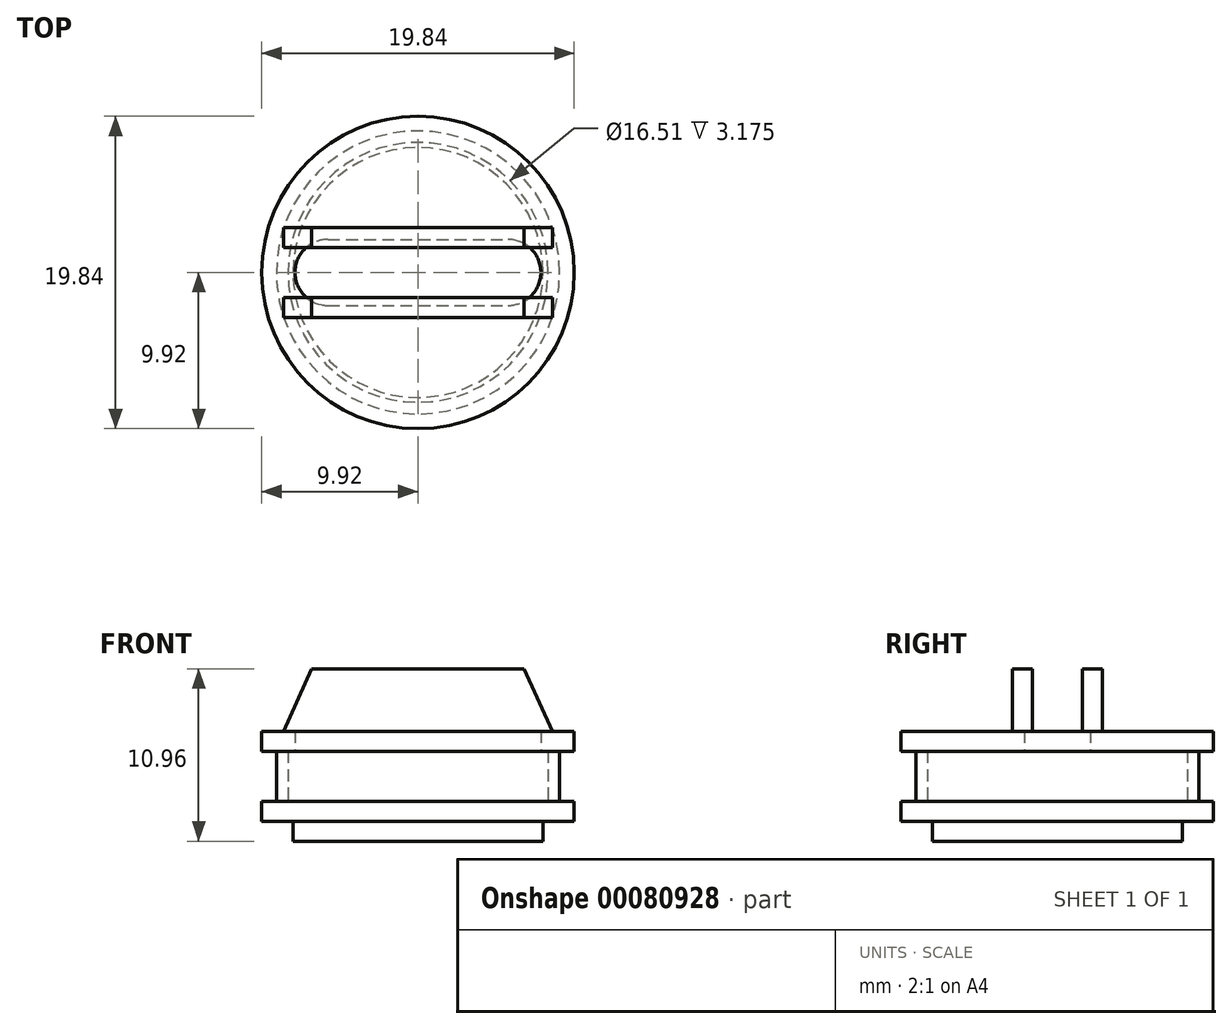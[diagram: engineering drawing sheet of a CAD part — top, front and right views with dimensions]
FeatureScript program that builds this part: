
annotation { "Feature Type Name" : "Feature", "Feature Type Description" : "" }
export const myFeature = defineFeature(function(context is Context, id is Id, definition is map)
    precondition{}
    {
        {
            var Q0;
            Q0=qCreatedBy(makeId("Top.planeOp"),FACE);
            var sketch = newSketch(context, id + "F0", { "sketchPlane" : qUnion([Q0])});
            skCircle(sketch, "E0", {"center": v(0, 0) * mm, "radius": 9.92 * mm});
            skCircle(sketch, "E1", {"center": v(0, 0) * mm, "radius": 9 * mm});
            skCircle(sketch, "E2", {"center": v(0, 0) * mm, "radius": 8.26 * mm});
            skLineSegment(sketch, "E3", {"start": v(-5.72, 2.1) * mm, "end": v(5.72, 2.1) * mm});
            skLineSegment(sketch, "E4", {"start": v(-5.72, -2.1) * mm, "end": v(5.72, -2.1) * mm});
            skArc(sketch, "E5", {"start": v(-5.72, 2.1) * mm, "mid": v(-7.81, 0) * mm, "end": v(-5.72, -2.1) * mm});
            skArc(sketch, "E6", {"start": v(5.72, 2.1) * mm, "mid": v(7.81, 0) * mm, "end": v(5.72, -2.1) * mm});
            skLineSegment(sketch, "E7", {"start": v(-5.72, 0) * mm, "end": v(5.72, 0) * mm, "construction": true});
            skSolve(sketch);
        }
        {
            var Q0;
            Q0=makeQuery(id+"F0.imprint","IMPRINT",FACE,{"disambiguationData":[TD([[makeQuery(id+"F0.imprint","IMPRINT",EDGE,{"derivedFrom":sQuery(id+"F0.wireOp",EDGE,"E0")}),1.0]])]});
            var Q1;
            Q1=makeQuery(id+"F0.imprint","IMPRINT",FACE,{"disambiguationData":[TD([[makeQuery(id+"F0.imprint","IMPRINT",EDGE,{"derivedFrom":sQuery(id+"F0.wireOp",EDGE,"E1")}),1.0]])]});
            var Q2;
            Q2=makeQuery(id+"F0.imprint","IMPRINT",FACE,{"disambiguationData":[TD([[makeQuery(id+"F0.imprint","IMPRINT",EDGE,{"derivedFrom":sQuery(id+"F0.wireOp",EDGE,"E2")}),1.0]])]});
            var Q3;
            Q3=makeQuery(id+"F0.imprint","IMPRINT",FACE,{"disambiguationData":[TD([[makeQuery(id+"F0.imprint","IMPRINT",EDGE,{"derivedFrom":sQuery(id+"F0.wireOp",EDGE,"E3")}),-1.0]])]});
            extrude(context, id + "F1", {"entities" : qUnion([Q0, Q1, Q2, Q3]), "oppositeDirection" : true, "depth" : 1.27 * mm});
        }
        {
            var Q0;
            Q0=makeQuery(id+"F1.opExtrude","CAP_FACE",FACE,{"disambiguationData":[OSD([sQuery(id+"F0.wireOp",EDGE,"E0")])],"isStart":false});
            cPlane(context, id + "F2", {"entities" : qUnion([Q0]), "cplaneType" : CPlaneType.OFFSET, "offset" : 0 * mm, "width" : 152.4 * mm, "height" : 152.4 * mm});
        }
        {
            var Q0;
            Q0=qCreatedBy(id+"F2.planeOp",FACE);
            var sketch = newSketch(context, id + "F3", { "sketchPlane" : qUnion([Q0])});
            skCircle(sketch, "E8", {"center": v(0, 0) * mm, "radius": 7.94 * mm});
            skSolve(sketch);
        }
        {
            var Q0;
            Q0=makeQuery(id+"F3.imprint","IMPRINT",FACE,{"disambiguationData":[TD([[makeQuery(id+"F3.imprint","IMPRINT",EDGE,{"derivedFrom":sQuery(id+"F3.wireOp",EDGE,"E8")}),1.0]])]});
            extrude(context, id + "F4", {"entities" : qUnion([Q0]), "depth" : 1.27 * mm});
        }
        {
            var Q0;
            Q0=makeQuery(id+"F0.imprint","IMPRINT",FACE,{"disambiguationData":[TD([[makeQuery(id+"F0.imprint","IMPRINT",EDGE,{"derivedFrom":sQuery(id+"F0.wireOp",EDGE,"E1")}),1.0]])]});
            extrude(context, id + "F5", {"entities" : qUnion([Q0]), "depth" : 3.17 * mm});
        }
        {
            var Q0;
            Q0=makeQuery(id+"F5.opExtrude","CAP_FACE",FACE,{"disambiguationData":[OSD([sQuery(id+"F0.wireOp",EDGE,"E1"),sQuery(id+"F0.wireOp",EDGE,"E2")])],"isStart":false});
            cPlane(context, id + "F6", {"entities" : qUnion([Q0]), "cplaneType" : CPlaneType.OFFSET, "offset" : 0 * mm, "width" : 152.4 * mm, "height" : 152.4 * mm});
        }
        {
            var Q0;
            Q0=qCreatedBy(id+"F6.planeOp",FACE);
            var sketch = newSketch(context, id + "F7", { "sketchPlane" : qUnion([Q0])});
            skCircle(sketch, "E9", {"center": v(0, 0) * mm, "radius": 9.92 * mm});
            skLineSegment(sketch, "E10", {"start": v(-5.72, 2.1) * mm, "end": v(5.72, 2.1) * mm});
            skLineSegment(sketch, "E11", {"start": v(-5.72, -2.1) * mm, "end": v(5.72, -2.1) * mm});
            skArc(sketch, "E12", {"start": v(-5.72, 2.1) * mm, "mid": v(-7.81, 0) * mm, "end": v(-5.72, -2.1) * mm});
            skArc(sketch, "E13", {"start": v(5.72, 2.1) * mm, "mid": v(7.81, 0) * mm, "end": v(5.72, -2.1) * mm});
            skLineSegment(sketch, "E14", {"start": v(-5.72, 0) * mm, "end": v(5.72, 0) * mm, "construction": true});
            skSolve(sketch);
        }
        {
            var Q0;
            Q0=makeQuery(id+"F7.imprint","IMPRINT",FACE,{"disambiguationData":[TD([[makeQuery(id+"F7.imprint","IMPRINT",EDGE,{"derivedFrom":sQuery(id+"F7.wireOp",EDGE,"E9")}),1.0]])]});
            extrude(context, id + "F8", {"entities" : qUnion([Q0]), "depth" : 1.27 * mm});
        }
        {
            var Q0;
            Q0=qCreatedBy(makeId("Front.planeOp"),FACE);
            cPlane(context, id + "F9", {"entities" : qUnion([Q0]), "cplaneType" : CPlaneType.OFFSET, "offset" : 1.59 * mm, "width" : 152.4 * mm, "height" : 152.4 * mm});
        }
        {
            var Q0;
            Q0=qCreatedBy(id+"F9.planeOp",FACE);
            var sketch = newSketch(context, id + "F10", { "sketchPlane" : qUnion([Q0])});
            skLineSegment(sketch, "E15", {"start": v(0, 0) * mm, "end": v(0, 10.06) * mm, "construction": true});
            skLineSegment(sketch, "E16", {"start": v(-6.75, 8.42) * mm, "end": v(6.75, 8.42) * mm});
            skLineSegment(sketch, "E17", {"start": v(6.75, 8.42) * mm, "end": v(8.53, 4.45) * mm});
            skLineSegment(sketch, "E18", {"start": v(8.53, 4.45) * mm, "end": v(-8.53, 4.44) * mm});
            skLineSegment(sketch, "E19", {"start": v(-8.53, 4.44) * mm, "end": v(-6.75, 8.42) * mm});
            skLineSegment(sketch, "E20", {"start": v(0, 8.42) * mm, "end": v(0, 4.45) * mm, "construction": true});
            skSolve(sketch);
        }
        {
            var Q0;
            Q0=makeQuery(id+"F10.imprint","IMPRINT",FACE,{"disambiguationData":[TD([[makeQuery(id+"F10.imprint","IMPRINT",EDGE,{"derivedFrom":sQuery(id+"F10.wireOp",EDGE,"E16")}),-1.0]])]});
            extrude(context, id + "F11", {"entities" : qUnion([Q0]), "depth" : 1.27 * mm});
        }
        {
            var Q0;
            Q0=makeQuery(id+"F11.opExtrude","SWEPT_BODY",BODY,{"disambiguationData":[OSD([sQuery(id+"F10.wireOp",EDGE,"E16"),sQuery(id+"F10.wireOp",EDGE,"E17"),sQuery(id+"F10.wireOp",EDGE,"E18"),sQuery(id+"F10.wireOp",EDGE,"E19")])]});
            var Q1;
            Q1=qCreatedBy(makeId("Front.planeOp"),FACE);
            mirror(context, id + "F12", {"operationType" : NewBodyOperationType.ADD, "entities" : qUnion([Q0]), "mirrorPlane" : qUnion([Q1])});
        }
    });
